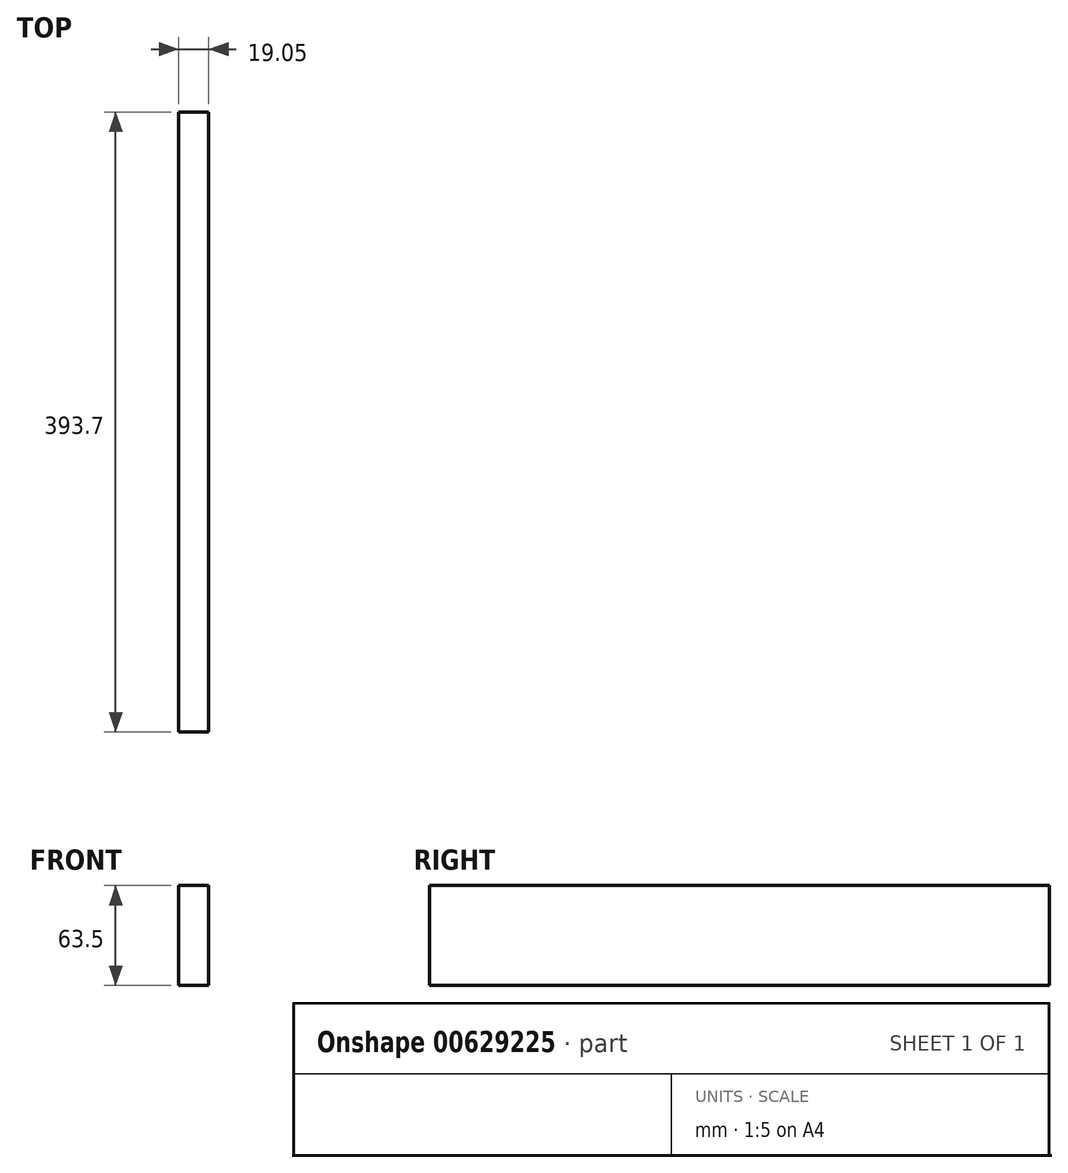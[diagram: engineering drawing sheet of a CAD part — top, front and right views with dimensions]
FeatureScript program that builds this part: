
annotation { "Feature Type Name" : "Feature", "Feature Type Description" : "" }
export const myFeature = defineFeature(function(context is Context, id is Id, definition is map)
    precondition{}
    {
        {
            var Q0;
            Q0=qCreatedBy(makeId("Right.planeOp"),FACE);
            var sketch = newSketch(context, id + "F0", { "sketchPlane" : qUnion([Q0])});
            skLineSegment(sketch, "E0.bottom", {"start": v(0, 0) * mm, "end": v(-393.7, 0) * mm});
            skLineSegment(sketch, "E0.top", {"start": v(0, 63.5) * mm, "end": v(-393.7, 63.5) * mm});
            skLineSegment(sketch, "E0.left", {"start": v(0, 0) * mm, "end": v(0, 63.5) * mm});
            skLineSegment(sketch, "E0.right", {"start": v(-393.7, 0) * mm, "end": v(-393.7, 63.5) * mm});
            skSolve(sketch);
        }
        {
            var Q0;
            Q0=makeQuery(id+"F0.imprint","IMPRINT",FACE,{"disambiguationData":[TD([[makeQuery(id+"F0.imprint","IMPRINT",EDGE,{"derivedFrom":sQuery(id+"F0.wireOp",EDGE,"E0.bottom")}),-1.0]])]});
            extrude(context, id + "F1", {"entities" : qUnion([Q0]), "depth" : 19.05 * mm, "offsetDistance" : 25.4 * mm});
        }
    });
